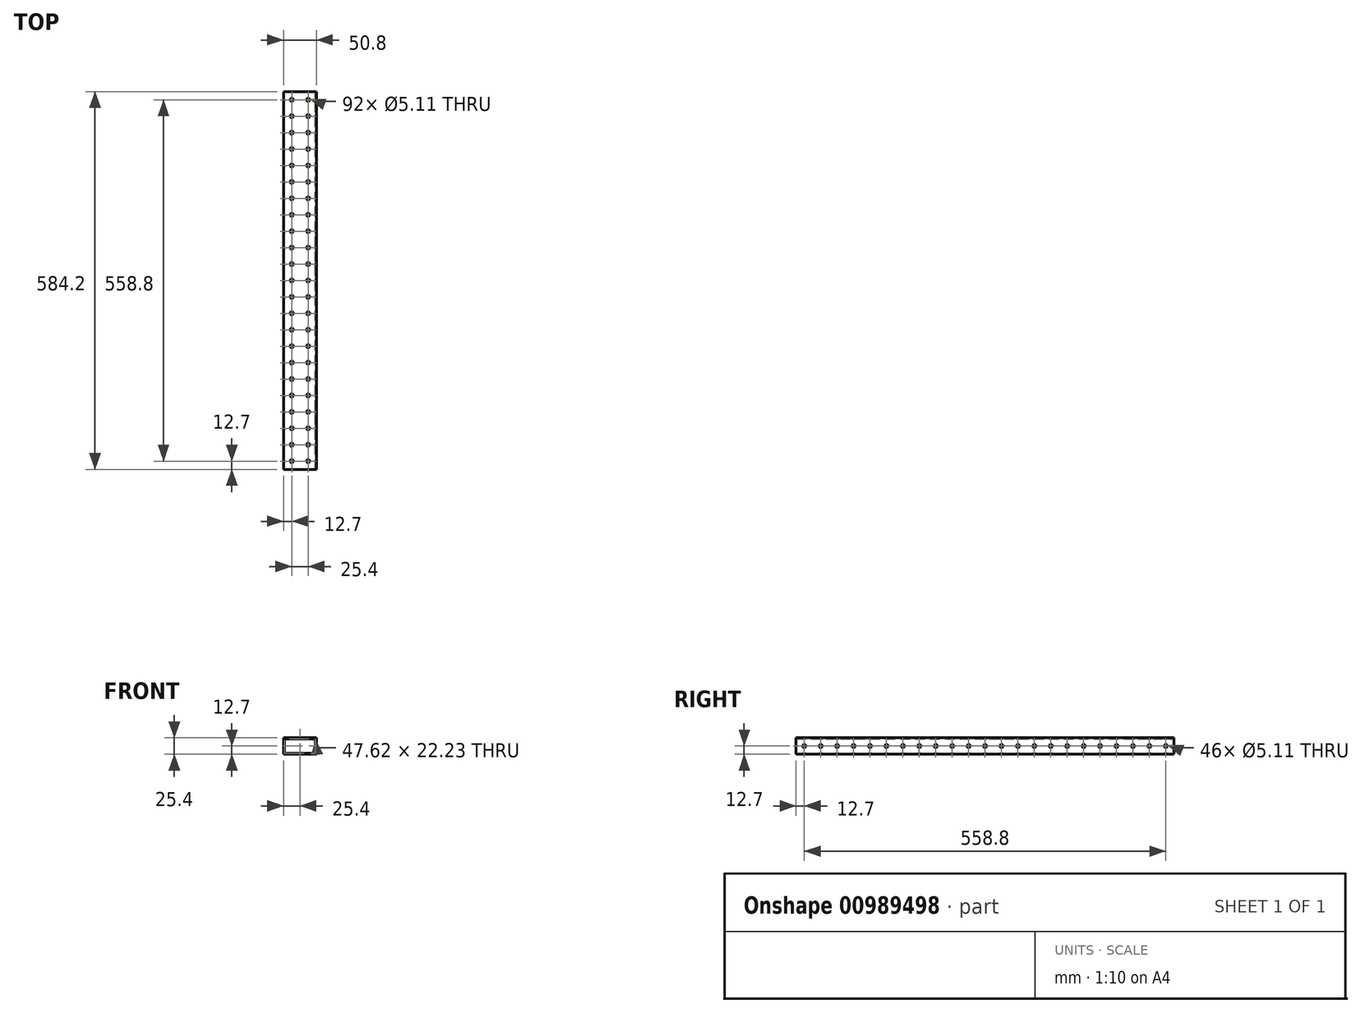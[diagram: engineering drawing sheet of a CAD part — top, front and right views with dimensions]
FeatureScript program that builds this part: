
annotation { "Feature Type Name" : "Feature", "Feature Type Description" : "" }
export const myFeature = defineFeature(function(context is Context, id is Id, definition is map)
    precondition{}
    {
        {
            var Q0;
            Q0=qCreatedBy(makeId("Front.planeOp"),FACE);
            var sketch = newSketch(context, id + "F0", { "sketchPlane" : qUnion([Q0])});
            skLineSegment(sketch, "E0.bottom", {"start": v(-25.4, 12.7) * mm, "end": v(25.4, 12.7) * mm});
            skLineSegment(sketch, "E0.top", {"start": v(-25.4, -12.7) * mm, "end": v(25.4, -12.7) * mm});
            skLineSegment(sketch, "E0.left", {"start": v(-25.4, 12.7) * mm, "end": v(-25.4, -12.7) * mm});
            skLineSegment(sketch, "E0.right", {"start": v(25.4, 12.7) * mm, "end": v(25.4, -12.7) * mm});
            skPoint(sketch, "E0.middle", {"position": v(0, 0) * mm});
            skLineSegment(sketch, "E1.0", {"start": v(-23.81, 11.11) * mm, "end": v(23.81, 11.11) * mm});
            skLineSegment(sketch, "E1.1", {"start": v(-23.81, 11.11) * mm, "end": v(-23.81, -11.11) * mm});
            skLineSegment(sketch, "E1.2", {"start": v(-23.81, -11.11) * mm, "end": v(23.81, -11.11) * mm});
            skLineSegment(sketch, "E1.3", {"start": v(23.81, 11.11) * mm, "end": v(23.81, -11.11) * mm});
            skSolve(sketch);
        }
        {
            var Q0;
            Q0 = qSketchRegion(id + "F0", true);
            extrude(context, id + "F1", {"entities" : qUnion([Q0]), "depth" : 584.2 * mm, "offsetDistance" : 25.4 * mm});
        }
        {
            var Q0;
            Q0=makeQuery(id+"F1.opExtrude","SWEPT_FACE",FACE,{"disambiguationData":[OSD([sQuery(id+"F0.wireOp",EDGE,"E0.bottom")])]});
            var sketch = newSketch(context, id + "F2", { "sketchPlane" : qUnion([Q0])});
            skCircle(sketch, "E2", {"center": v(-12.7, -12.7) * mm, "radius": 2.55 * mm});
            skCircle(sketch, "E3.0.1.0", {"center": v(-12.7, -38.1) * mm, "radius": 2.55 * mm});
            skCircle(sketch, "E3.0.2.0", {"center": v(-12.7, -63.5) * mm, "radius": 2.55 * mm});
            skCircle(sketch, "E3.0.3.0", {"center": v(-12.7, -88.9) * mm, "radius": 2.55 * mm});
            skCircle(sketch, "E3.0.4.0", {"center": v(-12.7, -114.3) * mm, "radius": 2.55 * mm});
            skCircle(sketch, "E3.0.5.0", {"center": v(-12.7, -139.7) * mm, "radius": 2.55 * mm});
            skCircle(sketch, "E3.0.6.0", {"center": v(-12.7, -165.1) * mm, "radius": 2.55 * mm});
            skCircle(sketch, "E3.0.7.0", {"center": v(-12.7, -190.5) * mm, "radius": 2.55 * mm});
            skCircle(sketch, "E3.0.8.0", {"center": v(-12.7, -215.9) * mm, "radius": 2.55 * mm});
            skCircle(sketch, "E3.0.9.0", {"center": v(-12.7, -241.3) * mm, "radius": 2.55 * mm});
            skCircle(sketch, "E3.0.10.0", {"center": v(-12.7, -266.7) * mm, "radius": 2.55 * mm});
            skCircle(sketch, "E3.0.11.0", {"center": v(-12.7, -292.1) * mm, "radius": 2.55 * mm});
            skCircle(sketch, "E3.0.12.0", {"center": v(-12.7, -317.5) * mm, "radius": 2.55 * mm});
            skCircle(sketch, "E3.0.13.0", {"center": v(-12.7, -342.9) * mm, "radius": 2.55 * mm});
            skCircle(sketch, "E3.0.14.0", {"center": v(-12.7, -368.3) * mm, "radius": 2.55 * mm});
            skCircle(sketch, "E3.0.15.0", {"center": v(-12.7, -393.7) * mm, "radius": 2.55 * mm});
            skCircle(sketch, "E3.0.16.0", {"center": v(-12.7, -419.1) * mm, "radius": 2.55 * mm});
            skCircle(sketch, "E3.0.17.0", {"center": v(-12.7, -444.5) * mm, "radius": 2.55 * mm});
            skCircle(sketch, "E3.0.18.0", {"center": v(-12.7, -469.9) * mm, "radius": 2.55 * mm});
            skCircle(sketch, "E3.0.19.0", {"center": v(-12.7, -495.3) * mm, "radius": 2.55 * mm});
            skCircle(sketch, "E3.0.20.0", {"center": v(-12.7, -520.7) * mm, "radius": 2.55 * mm});
            skCircle(sketch, "E3.0.21.0", {"center": v(-12.7, -546.1) * mm, "radius": 2.55 * mm});
            skCircle(sketch, "E3.0.22.0", {"center": v(-12.7, -571.5) * mm, "radius": 2.55 * mm});
            skCircle(sketch, "E3.1.0.0", {"center": v(12.7, -12.7) * mm, "radius": 2.55 * mm});
            skCircle(sketch, "E3.1.1.0", {"center": v(12.7, -38.1) * mm, "radius": 2.55 * mm});
            skCircle(sketch, "E3.1.2.0", {"center": v(12.7, -63.5) * mm, "radius": 2.55 * mm});
            skCircle(sketch, "E3.1.3.0", {"center": v(12.7, -88.9) * mm, "radius": 2.55 * mm});
            skCircle(sketch, "E3.1.4.0", {"center": v(12.7, -114.3) * mm, "radius": 2.55 * mm});
            skCircle(sketch, "E3.1.5.0", {"center": v(12.7, -139.7) * mm, "radius": 2.55 * mm});
            skCircle(sketch, "E3.1.6.0", {"center": v(12.7, -165.1) * mm, "radius": 2.55 * mm});
            skCircle(sketch, "E3.1.7.0", {"center": v(12.7, -190.5) * mm, "radius": 2.55 * mm});
            skCircle(sketch, "E3.1.8.0", {"center": v(12.7, -215.9) * mm, "radius": 2.55 * mm});
            skCircle(sketch, "E3.1.9.0", {"center": v(12.7, -241.3) * mm, "radius": 2.55 * mm});
            skCircle(sketch, "E3.1.10.0", {"center": v(12.7, -266.7) * mm, "radius": 2.55 * mm});
            skCircle(sketch, "E3.1.11.0", {"center": v(12.7, -292.1) * mm, "radius": 2.55 * mm});
            skCircle(sketch, "E3.1.12.0", {"center": v(12.7, -317.5) * mm, "radius": 2.55 * mm});
            skCircle(sketch, "E3.1.13.0", {"center": v(12.7, -342.9) * mm, "radius": 2.55 * mm});
            skCircle(sketch, "E3.1.14.0", {"center": v(12.7, -368.3) * mm, "radius": 2.55 * mm});
            skCircle(sketch, "E3.1.15.0", {"center": v(12.7, -393.7) * mm, "radius": 2.55 * mm});
            skCircle(sketch, "E3.1.16.0", {"center": v(12.7, -419.1) * mm, "radius": 2.55 * mm});
            skCircle(sketch, "E3.1.17.0", {"center": v(12.7, -444.5) * mm, "radius": 2.55 * mm});
            skCircle(sketch, "E3.1.18.0", {"center": v(12.7, -469.9) * mm, "radius": 2.55 * mm});
            skCircle(sketch, "E3.1.19.0", {"center": v(12.7, -495.3) * mm, "radius": 2.55 * mm});
            skCircle(sketch, "E3.1.20.0", {"center": v(12.7, -520.7) * mm, "radius": 2.55 * mm});
            skCircle(sketch, "E3.1.21.0", {"center": v(12.7, -546.1) * mm, "radius": 2.55 * mm});
            skCircle(sketch, "E3.1.22.0", {"center": v(12.7, -571.5) * mm, "radius": 2.55 * mm});
            skLineSegment(sketch, "E3.direction1", {"start": v(-12.7, -12.7) * mm, "end": v(12.7, -12.7) * mm, "construction": true});
            skLineSegment(sketch, "E3.direction2", {"start": v(-12.7, -12.7) * mm, "end": v(-12.7, -38.1) * mm, "construction": true});
            skSolve(sketch);
        }
        {
            var Q0;
            Q0 = qSketchRegion(id + "F2", true);
            extrude(context, id + "F3", {"entities" : qUnion([Q0]), "operationType" : NewBodyOperationType.REMOVE, "oppositeDirection" : true, "depth" : 25.4 * mm, "offsetDistance" : 25.4 * mm});
        }
        {
            var Q0;
            Q0=makeQuery(id+"F1.opExtrude","SWEPT_FACE",FACE,{"disambiguationData":[OSD([sQuery(id+"F0.wireOp",EDGE,"E0.left")])]});
            var sketch = newSketch(context, id + "F4", { "sketchPlane" : qUnion([Q0])});
            skCircle(sketch, "E4", {"center": v(12.7, 0) * mm, "radius": 2.55 * mm});
            skCircle(sketch, "E5.1.0.0", {"center": v(38.1, 0) * mm, "radius": 2.55 * mm});
            skCircle(sketch, "E5.2.0.0", {"center": v(63.5, 0) * mm, "radius": 2.55 * mm});
            skCircle(sketch, "E5.3.0.0", {"center": v(88.9, 0) * mm, "radius": 2.55 * mm});
            skCircle(sketch, "E5.4.0.0", {"center": v(114.3, 0) * mm, "radius": 2.55 * mm});
            skCircle(sketch, "E5.5.0.0", {"center": v(139.7, 0) * mm, "radius": 2.55 * mm});
            skCircle(sketch, "E5.6.0.0", {"center": v(165.1, 0) * mm, "radius": 2.55 * mm});
            skCircle(sketch, "E5.7.0.0", {"center": v(190.5, 0) * mm, "radius": 2.55 * mm});
            skCircle(sketch, "E5.8.0.0", {"center": v(215.9, 0) * mm, "radius": 2.55 * mm});
            skCircle(sketch, "E5.9.0.0", {"center": v(241.3, 0) * mm, "radius": 2.55 * mm});
            skCircle(sketch, "E5.10.0.0", {"center": v(266.7, 0) * mm, "radius": 2.55 * mm});
            skCircle(sketch, "E5.11.0.0", {"center": v(292.1, 0) * mm, "radius": 2.55 * mm});
            skCircle(sketch, "E5.12.0.0", {"center": v(317.5, 0) * mm, "radius": 2.55 * mm});
            skCircle(sketch, "E5.13.0.0", {"center": v(342.9, 0) * mm, "radius": 2.55 * mm});
            skCircle(sketch, "E5.14.0.0", {"center": v(368.3, 0) * mm, "radius": 2.55 * mm});
            skCircle(sketch, "E5.15.0.0", {"center": v(393.7, 0) * mm, "radius": 2.55 * mm});
            skCircle(sketch, "E5.16.0.0", {"center": v(419.1, 0) * mm, "radius": 2.55 * mm});
            skCircle(sketch, "E5.17.0.0", {"center": v(444.5, 0) * mm, "radius": 2.55 * mm});
            skCircle(sketch, "E5.18.0.0", {"center": v(469.9, 0) * mm, "radius": 2.55 * mm});
            skCircle(sketch, "E5.19.0.0", {"center": v(495.3, 0) * mm, "radius": 2.55 * mm});
            skCircle(sketch, "E5.20.0.0", {"center": v(520.7, 0) * mm, "radius": 2.55 * mm});
            skCircle(sketch, "E5.21.0.0", {"center": v(546.1, 0) * mm, "radius": 2.55 * mm});
            skCircle(sketch, "E5.22.0.0", {"center": v(571.5, 0) * mm, "radius": 2.55 * mm});
            skLineSegment(sketch, "E5.direction1", {"start": v(12.7, 0) * mm, "end": v(38.1, 0) * mm, "construction": true});
            skSolve(sketch);
        }
        {
            var Q0;
            Q0 = qSketchRegion(id + "F4", true);
            extrude(context, id + "F5", {"entities" : qUnion([Q0]), "operationType" : NewBodyOperationType.REMOVE, "endBound" : BoundingType.THROUGH_ALL, "oppositeDirection" : true, "depth" : 25.4 * mm, "offsetDistance" : 25.4 * mm});
        }
    });
